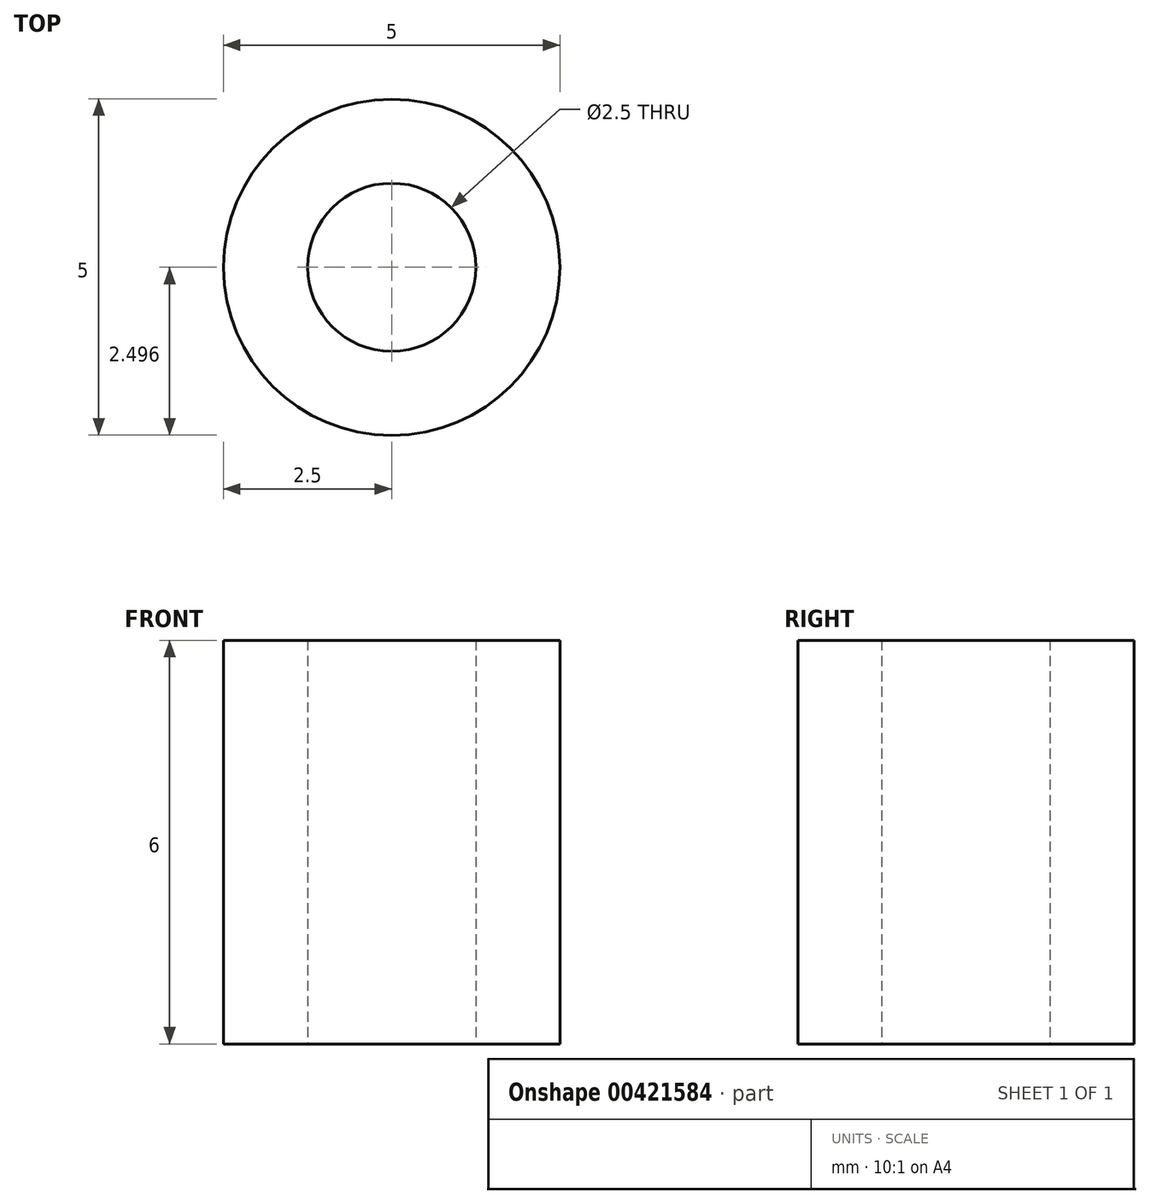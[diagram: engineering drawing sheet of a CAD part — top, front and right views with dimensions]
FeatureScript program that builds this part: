
annotation { "Feature Type Name" : "Feature", "Feature Type Description" : "" }
export const myFeature = defineFeature(function(context is Context, id is Id, definition is map)
    precondition{}
    {
        {
            var Q0;
            Q0=qCreatedBy(makeId("Top.planeOp"),FACE);
            var sketch = newSketch(context, id + "F0", { "sketchPlane" : qUnion([Q0])});
            skCircle(sketch, "E0", {"center": v(-77.23, -34.87) * mm, "radius": 1.25 * mm});
            skCircle(sketch, "E1", {"center": v(-77.23, -34.87) * mm, "radius": 2.5 * mm});
            skSolve(sketch);
        }
        {
            var Q0;
            Q0 = qSketchRegion(id + "F0", true);
            extrude(context, id + "F1", {"entities" : qUnion([Q0]), "depth" : 6 * mm, "offsetDistance" : 25 * mm});
        }
    });
